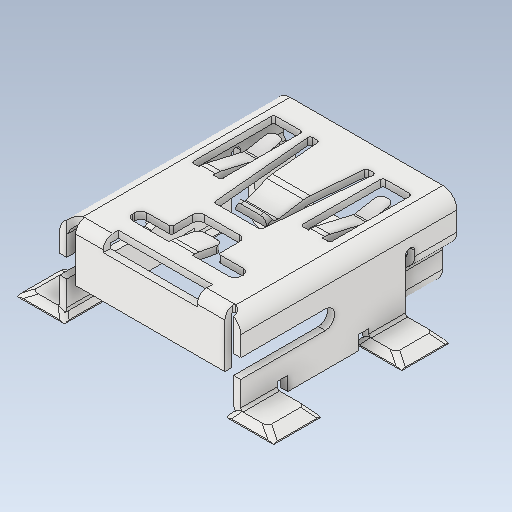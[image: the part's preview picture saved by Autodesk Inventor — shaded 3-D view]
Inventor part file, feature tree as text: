
AUTODESK INVENTOR PART (.ipt)
format: ipt  version: 2020.1 (Build 241239000, 239)  size: 392,704 bytes
history: native  units: mm
features: fillet x1
ambient origin geometry x8: Origin, YZ Plane, XZ Plane, XY Plane, X Axis, Y Axis, Z Axis, Center Point
bodies: Solid1 (feature_tree)
feature tree (1):
  fillet  "Fillet14"  [1 undecoded]
note: 1 required parameter value undecoded (feature->parameter linkage not recoverable at this tier; creation-order binding heuristic only, values carry confidence <= 0.55)
